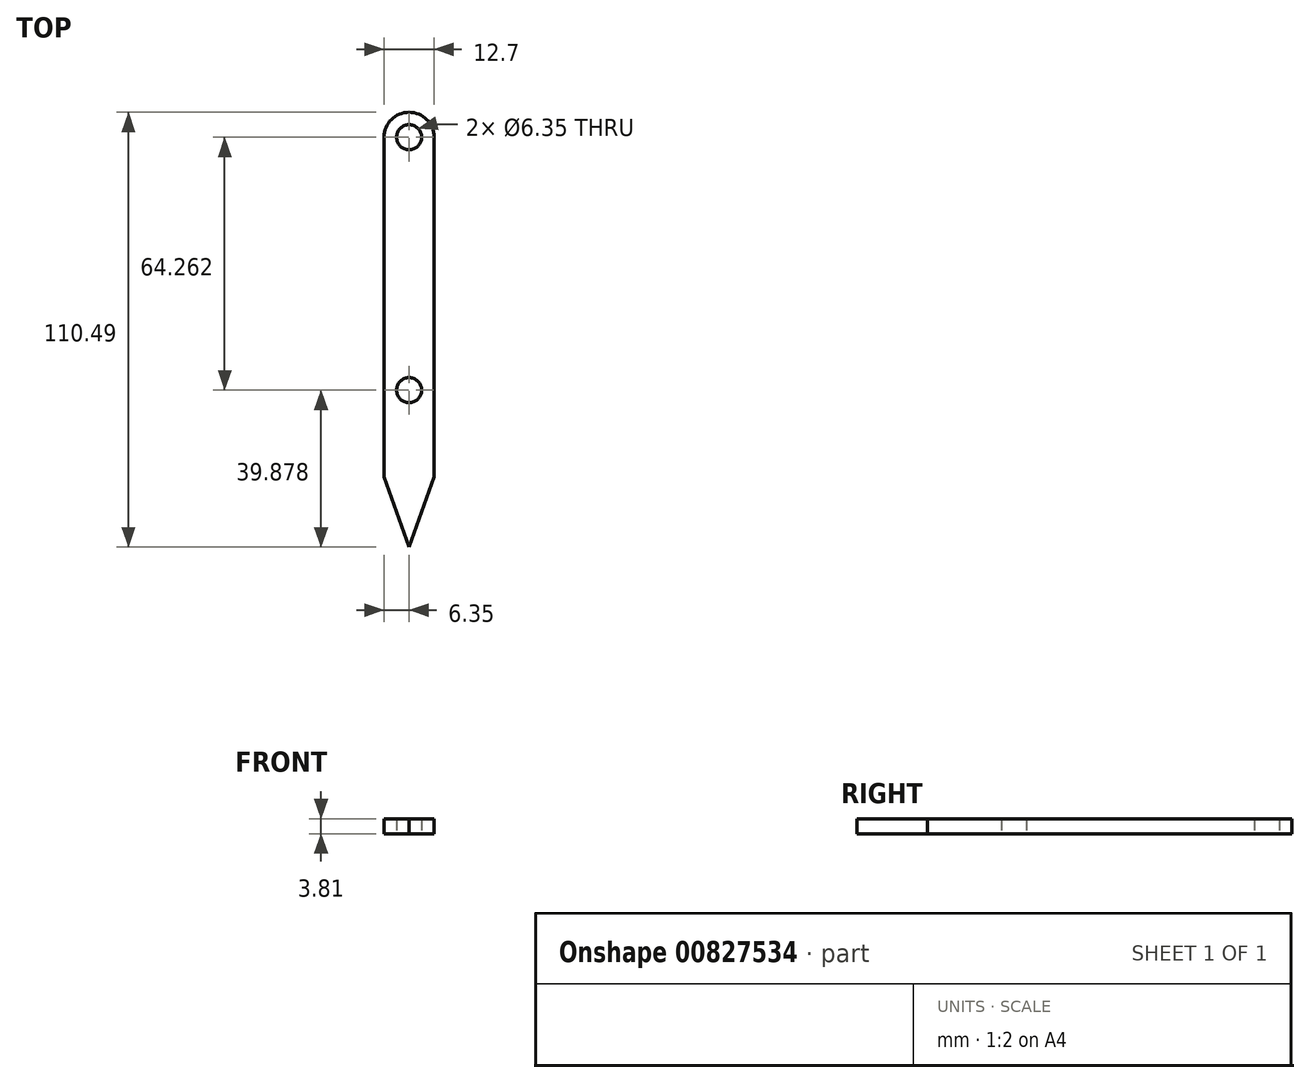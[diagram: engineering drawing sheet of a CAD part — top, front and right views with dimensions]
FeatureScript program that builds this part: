
annotation { "Feature Type Name" : "Feature", "Feature Type Description" : "" }
export const myFeature = defineFeature(function(context is Context, id is Id, definition is map)
    precondition{}
    {
        {
            var Q0;
            Q0=qCreatedBy(makeId("Top.planeOp"),FACE);
            var sketch = newSketch(context, id + "F0", { "sketchPlane" : qUnion([Q0])});
            skLineSegment(sketch, "E0.bottom", {"start": v(-6.35, 52.07) * mm, "end": v(6.35, 52.07) * mm});
            skLineSegment(sketch, "E0.top", {"start": v(-6.35, -52.07) * mm, "end": v(6.35, -52.07) * mm});
            skLineSegment(sketch, "E0.left", {"start": v(-6.35, 52.07) * mm, "end": v(-6.35, -52.07) * mm});
            skLineSegment(sketch, "E0.right", {"start": v(6.35, 52.07) * mm, "end": v(6.35, -52.07) * mm});
            skPoint(sketch, "E0.middle", {"position": v(0, 0) * mm});
            skCircle(sketch, "E1", {"center": v(0, 52.07) * mm, "radius": 3.18 * mm});
            skArc(sketch, "E2", {"start": v(6.35, 52.07) * mm, "mid": v(0, 58.42) * mm, "end": v(-6.35, 52.07) * mm});
            skLineSegment(sketch, "E3", {"start": v(0, -52.07) * mm, "end": v(-6.35, -34.23) * mm});
            skLineSegment(sketch, "E4", {"start": v(-6.35, -34.23) * mm, "end": v(6.35, -34.23) * mm});
            skLineSegment(sketch, "E5", {"start": v(6.35, -34.23) * mm, "end": v(0, -52.07) * mm});
            skCircle(sketch, "E6", {"center": v(0, -12.2) * mm, "radius": 3.18 * mm});
            skSolve(sketch);
        }
        {
            var Q0;
            {var subQ4=sQuery(id+"F0.wireOp",EDGE,"VFi7OpaB-yLmy-tm1l-0o5h-QAqS6r32s6S1");Q0=makeQuery(id+"F0.imprint","IMPRINT",FACE,{"disambiguationData":[TD([[makeQuery(id+"F0.imprint","IMPRINT",EDGE,{"derivedFrom":subQ4}),1.0]])]});}
            var Q1;
            Q1=makeQuery(id+"F0.imprint","IMPRINT",FACE,{"disambiguationData":[TD([[makeQuery(id+"F0.imprint","IMPRINT",EDGE,{"derivedFrom":sQuery(id+"F0.wireOp",EDGE,"m02FCX0K-uOYu-MlxC-pXOf-QfYkZrp66M1T")}),-1.0]])]});
            var Q2;
            {var subQ0=sQuery(id+"F0.wireOp",EDGE,"E2");Q2=makeQuery(id+"F0.imprint","IMPRINT",FACE,{"disambiguationData":[TD([[makeQuery(id+"F0.imprint","IMPRINT",EDGE,{"derivedFrom":subQ0}),1.0]])]});}
            extrude(context, id + "F1", {"entities" : qUnion([Q0, Q1, Q2]), "depth" : 3.8 * mm, "offsetDistance" : 25.4 * mm});
        }
        {
            var Q0;
            Q0=makeQuery(id+"F0.imprint","IMPRINT",FACE,{"disambiguationData":[TD([[makeQuery(id+"F0.imprint","IMPRINT",EDGE,{"derivedFrom":sQuery(id+"F0.wireOp",EDGE,"E3")}),-1.0]])]});
            var Q1;
            {var subQ4=sQuery(id+"F0.wireOp",EDGE,"E4");Q1=makeQuery(id+"F0.imprint","IMPRINT",FACE,{"disambiguationData":[TD([[makeQuery(id+"F0.imprint","IMPRINT",EDGE,{"derivedFrom":subQ4}),1.0]])]});}
            extrude(context, id + "F2", {"entities" : qUnion([Q0, Q1]), "operationType" : NewBodyOperationType.ADD, "depth" : 3.8 * mm, "offsetDistance" : 25.4 * mm});
        }
    });
